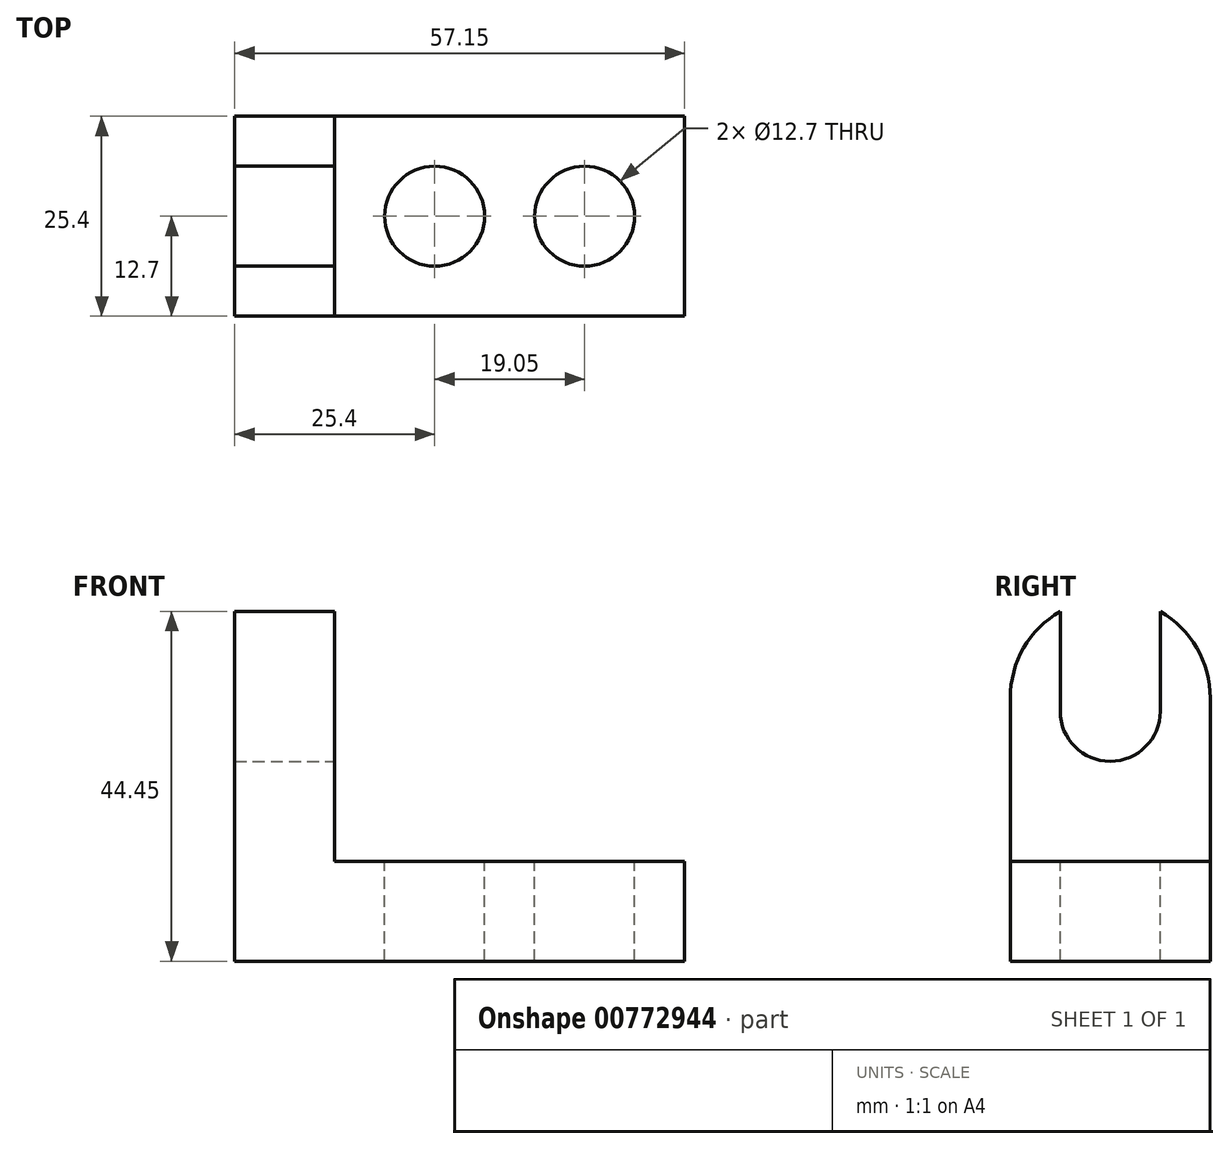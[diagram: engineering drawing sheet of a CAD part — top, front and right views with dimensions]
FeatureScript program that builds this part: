
annotation { "Feature Type Name" : "Feature", "Feature Type Description" : "" }
export const myFeature = defineFeature(function(context is Context, id is Id, definition is map)
    precondition{}
    {
        {
            var Q0;
            Q0=qCreatedBy(makeId("Front.planeOp"),FACE);
            var sketch = newSketch(context, id + "F0", { "sketchPlane" : qUnion([Q0])});
            skLineSegment(sketch, "E0", {"start": v(0, 0) * mm, "end": v(57.15, 0) * mm});
            skLineSegment(sketch, "E1", {"start": v(57.15, 0) * mm, "end": v(57.15, 44.45) * mm});
            skLineSegment(sketch, "E2", {"start": v(57.15, 44.45) * mm, "end": v(0, 44.45) * mm});
            skLineSegment(sketch, "E3", {"start": v(0, 44.45) * mm, "end": v(0, 0) * mm});
            skSolve(sketch);
        }
        {
            var Q0;
            Q0=makeQuery(id+"F0.imprint","IMPRINT",FACE,{"disambiguationData":[TD([[makeQuery(id+"F0.imprint","IMPRINT",EDGE,{"derivedFrom":sQuery(id+"F0.wireOp",EDGE,"E0")}),1.0]])]});
            extrude(context, id + "F1", {"entities" : qUnion([Q0]), "depth" : 25.4 * mm, "offsetDistance" : 25.4 * mm});
        }
        {
            var Q0;
            Q0=makeQuery(id+"F1.opExtrude","CAP_FACE",FACE,{"disambiguationData":[OSD([sQuery(id+"F0.wireOp",EDGE,"E0"),sQuery(id+"F0.wireOp",EDGE,"E1"),sQuery(id+"F0.wireOp",EDGE,"E2"),sQuery(id+"F0.wireOp",EDGE,"E3")])],"isStart":false});
            var sketch = newSketch(context, id + "F2", { "sketchPlane" : qUnion([Q0])});
            skLineSegment(sketch, "E4", {"start": v(12.7, 44.45) * mm, "end": v(12.7, 12.7) * mm});
            skLineSegment(sketch, "E5", {"start": v(12.7, 12.7) * mm, "end": v(57.15, 12.7) * mm});
            skLineSegment(sketch, "E6", {"start": v(57.15, 12.7) * mm, "end": v(57.15, 44.45) * mm});
            skLineSegment(sketch, "E7", {"start": v(57.15, 44.45) * mm, "end": v(12.7, 44.45) * mm});
            skSolve(sketch);
        }
        {
            var Q0;
            Q0=makeQuery(id+"F2.imprint","IMPRINT",FACE,{"disambiguationData":[TD([[makeQuery(id+"F2.imprint","IMPRINT",EDGE,{"derivedFrom":sQuery(id+"F2.wireOp",EDGE,"E4")}),1.0]])]});
            extrude(context, id + "F3", {"entities" : qUnion([Q0]), "operationType" : NewBodyOperationType.REMOVE, "oppositeDirection" : true, "depth" : 25.4 * mm, "offsetDistance" : 25.4 * mm});
        }
        {
            var Q0;
            Q0=makeQuery(id+"F3.boolean.opBoolean","COPY",FACE,{"derivedFrom":makeQuery(id+"F3.opExtrude","SWEPT_FACE",FACE,{"disambiguationData":[OSD([sQuery(id+"F2.wireOp",EDGE,"E5")])]})});
            var sketch = newSketch(context, id + "F4", { "sketchPlane" : qUnion([Q0])});
            skCircle(sketch, "E8", {"center": v(25.4, -12.7) * mm, "radius": 6.35 * mm});
            skCircle(sketch, "E9", {"center": v(44.45, -12.7) * mm, "radius": 6.35 * mm});
            skSolve(sketch);
        }
        {
            var Q0;
            Q0=makeQuery(id+"F4.imprint","IMPRINT",FACE,{"disambiguationData":[TD([[makeQuery(id+"F4.imprint","IMPRINT",EDGE,{"derivedFrom":sQuery(id+"F4.wireOp",EDGE,"E8")}),1.0]])]});
            var Q1;
            Q1=makeQuery(id+"F4.imprint","IMPRINT",FACE,{"disambiguationData":[TD([[makeQuery(id+"F4.imprint","IMPRINT",EDGE,{"derivedFrom":sQuery(id+"F4.wireOp",EDGE,"E9")}),1.0]])]});
            extrude(context, id + "F5", {"entities" : qUnion([Q0, Q1]), "operationType" : NewBodyOperationType.REMOVE, "oppositeDirection" : true, "depth" : 25.4 * mm, "offsetDistance" : 25.4 * mm});
        }
        {
            var Q0;
            Q0=makeQuery(id+"F3.boolean.opBoolean","COPY",FACE,{"derivedFrom":makeQuery(id+"F3.opExtrude","SWEPT_FACE",FACE,{"disambiguationData":[OSD([sQuery(id+"F2.wireOp",EDGE,"E4")])]})});
            var sketch = newSketch(context, id + "F6", { "sketchPlane" : qUnion([Q0])});
            skCircle(sketch, "E10", {"center": v(-12.7, 31.75) * mm, "radius": 6.35 * mm});
            skLineSegment(sketch, "E11", {"start": v(-6.35, 31.75) * mm, "end": v(-6.35, 44.45) * mm});
            skLineSegment(sketch, "E12", {"start": v(-19.05, 31.75) * mm, "end": v(-19.05, 44.45) * mm});
            skLineSegment(sketch, "E13", {"start": v(-19.05, 44.45) * mm, "end": v(-6.35, 44.45) * mm});
            skSolve(sketch);
        }
        {
            var Q0;
            {var subQ0=sQuery(id+"F6.wireOp",EDGE,"E11");Q0=makeQuery(id+"F6.imprint","IMPRINT",FACE,{"disambiguationData":[TD([[makeQuery(id+"F6.imprint","IMPRINT",EDGE,{"derivedFrom":subQ0}),1.0]])]});}
            var Q1;
            {var subQ0=sQuery(id+"F6.wireOp",EDGE,"E10");var subQ1=makeQuery(id+"F6.imprint","INTERSECT",VERTEX,{"derivedFrom":[subQ0,sQuery(id+"F6.wireOp",EDGE,"E11")]});Q1=makeQuery(id+"F6.imprint","IMPRINT",FACE,{"disambiguationData":[TD([[makeQuery(id+"F6.imprint","IMPRINT",EDGE,{"disambiguationData":[TD([[subQ1,-1.0]])],"derivedFrom":subQ0}),1.0]])]});}
            extrude(context, id + "F7", {"entities" : qUnion([Q0, Q1]), "operationType" : NewBodyOperationType.REMOVE, "oppositeDirection" : true, "depth" : 25.4 * mm, "offsetDistance" : 25.4 * mm});
        }
        {
            var Q0;
            Q0=makeQuery(id+"F1.opExtrude","CAP_EDGE",EDGE,{"disambiguationData":[OSD([sQuery(id+"F0.wireOp",EDGE,"E2")])],"isStart":false});
            var Q1;
            Q1=makeQuery(id+"F1.opExtrude","CAP_EDGE",EDGE,{"disambiguationData":[OSD([sQuery(id+"F0.wireOp",EDGE,"E2")])],"isStart":true});
            fillet(context, id + "F8", {"entities" : qUnion([Q0, Q1]), "radius" : 12.7 * mm, "tangentPropagation" : true, "allowEdgeOverflow" : false});
        }
    });
